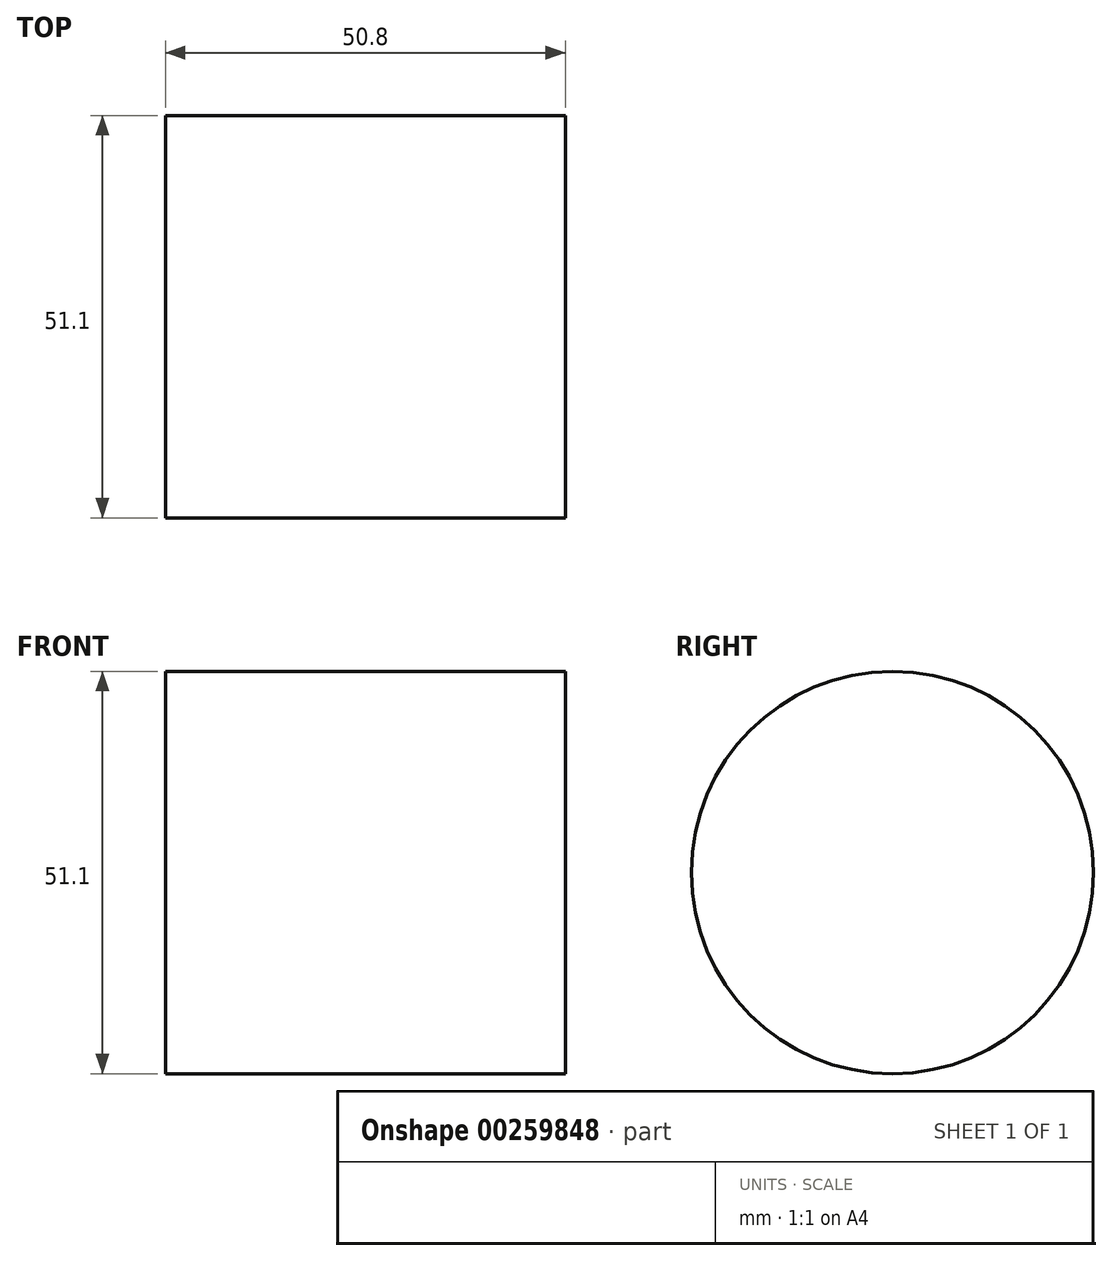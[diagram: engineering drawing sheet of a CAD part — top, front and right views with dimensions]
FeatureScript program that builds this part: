
annotation { "Feature Type Name" : "Feature", "Feature Type Description" : "" }
export const myFeature = defineFeature(function(context is Context, id is Id, definition is map)
    precondition{}
    {
        {
            var Q0;
            Q0=qCreatedBy(makeId("Right.planeOp"),FACE);
            var sketch = newSketch(context, id + "F0", { "sketchPlane" : qUnion([Q0])});
            skCircle(sketch, "E0", {"center": v(0, 0) * mm, "radius": 25.55 * mm});
            skSolve(sketch);
        }
        {
            var Q0;
            Q0 = qSketchRegion(id + "F0", true);
            extrude(context, id + "F1", {"entities" : qUnion([Q0]), "depth" : 50.8 * mm});
        }
    });
